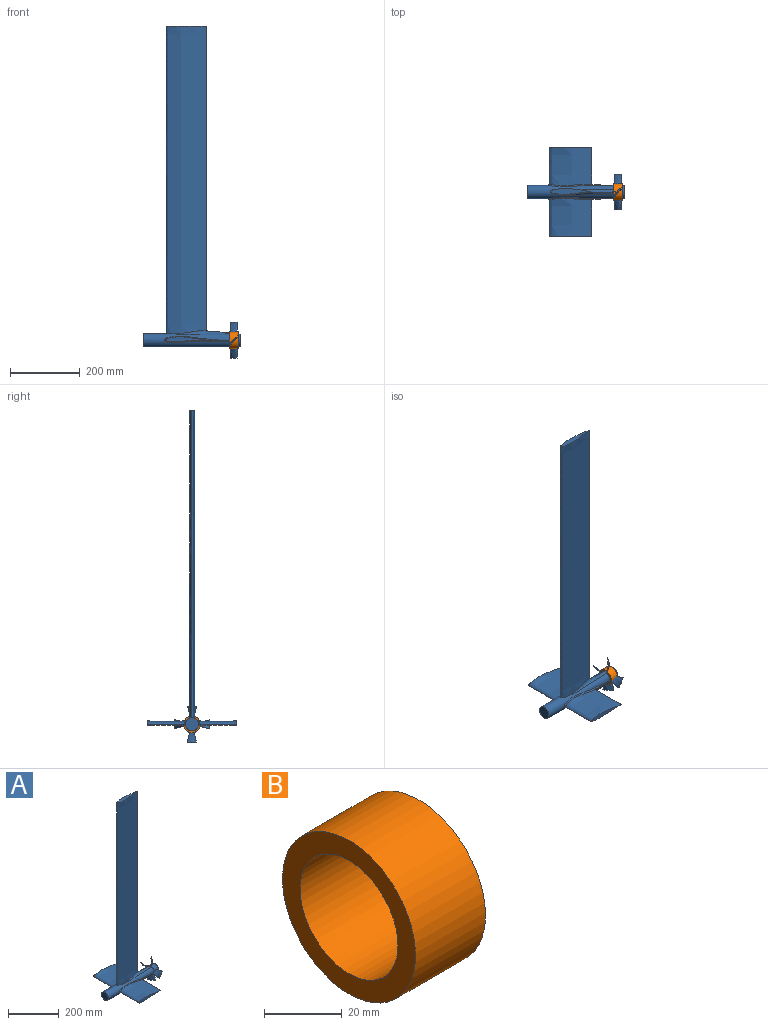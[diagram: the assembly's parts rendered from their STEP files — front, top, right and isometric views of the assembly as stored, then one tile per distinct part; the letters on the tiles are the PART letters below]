
ASSEMBLY  parts=2 mates=1
PART A: 35 faces, bbox 313.5x254.6x950.5 mm
  f0: plane 20.88x15.27mm, normal (1,0,0), area 34.3mm2, adj f6,f15,f21,f30,f32
  f1: plane 20.86x18.71mm, normal (1,0,0), area 44.7mm2, adj f6,f15,f20,f21,f27,f29
  f2: plane 20.54x15.24mm, normal (1,0,0), area 34.1mm2, adj f6,f21,f24,f26
  f3: extruded ~881.15x119.21mm, area 102994.5mm2, adj f4,f5,f15,f20
  f4: extruded ~880.11x115.56mm, area 103673mm2, adj f3,f5,f15
  f5: plane 115.59x15.95mm, normal (0,0,1), area 1218.9mm2, adj f3,f4
  f6: cylinder r=19.05mm len=254mm, axis (-1,0,0), area 23671.1mm2, adj f0,f1,f2,f7,f8,f15,f16,f17
  f7: plane 20.54x15.24mm, normal (1,0,0), area 34.1mm2, adj f6,f21,f23,f33
  f8: plane 38.1x38.1mm, normal (-1,0,0), area 1140.1mm2, adj f6
  f9: plane 120.65x12.89mm, normal (0,1,0), area 984.2mm2, adj f10,f11
  f10: extruded ~120.65x105.16mm, area 12739.2mm2, adj f9,f11,f16,f17
  f11: extruded ~120.65x104.46mm, area 12900mm2, adj f9,f10,f16
  f12: plane 120.67x12.89mm, normal (0,-1,0), area 984.2mm2, adj f13,f14
  f13: extruded ~120.65x105.16mm, area 12739.2mm2, adj f12,f14,f18,f19
  f14: extruded ~120.65x104.46mm, area 12900mm2, adj f12,f13,f19
  f15: bspline ~246.87x15.23mm, area 1459.2mm2, adj f0,f1,f3,f4,f6,f20,f29,f30
  f16: bspline ~202.66x19.82mm, area 667.5mm2, adj f6,f10,f11,f17
  f17: bspline ~228.56x6.02mm, area 809.6mm2, adj f6,f10,f16
  f18: bspline ~228.56x6.02mm, area 752.8mm2, adj f6,f13,f19,f32
  f19: bspline ~202.66x19.82mm, area 667.5mm2, adj f6,f13,f14,f18,f32
  f20: bspline ~193.83x13.44mm, area 947.7mm2, adj f1,f3,f6,f15
  f21: cylinder r=17.78mm len=35.56mm, axis (-1,0,0), area 2775.2mm2, adj f0,f1,f2,f7,f22,f23,f24,f26
  f22: plane 35.56x35.56mm, normal (1,0,0), area 993.1mm2, adj f21
  f23: bspline ~33.51x25.77mm, area 881.3mm2, adj f6,f7,f21,f24,f25
  f24: bspline ~50.8x25.79mm, area 873.7mm2, adj f2,f6,f21,f23,f25
  f25: plane 26.36x19.69mm, normal (0,0,-1), area 67.5mm2, adj f23,f24
  f26: bspline ~33.51x25.77mm, area 881.3mm2, adj f2,f6,f21,f27,f28
  f27: bspline ~50.8x25.79mm, area 873.7mm2, adj f1,f6,f21,f26,f28
  f28: plane 26.36x19.69mm, normal (0,1,0), area 67.5mm2, adj f26,f27
  f29: bspline ~33.51x25.77mm, area 878.8mm2, adj f1,f15,f21,f30,f31
  f30: bspline ~50.8x25.79mm, area 873mm2, adj f0,f15,f21,f29,f31
  f31: plane 26.01x19.34mm, normal (0,0,1), area 67.5mm2, adj f29,f30
  f32: bspline ~50.8x25.77mm, area 880.8mm2, adj f0,f6,f18,f19,f21,f33,f34
  f33: bspline ~50.8x25.79mm, area 873.7mm2, adj f6,f7,f21,f32,f34
  f34: plane 25.99x19.32mm, normal (0,-1,0), area 67.5mm2, adj f32,f33
PART B: 4 faces, bbox 25.4x48.3x48.3 mm
  f0: cylinder r=17.78mm len=35.56mm, axis (-1,0,0), area 2837.6mm2, adj f2,f3
  f1: cylinder r=24.13mm len=48.26mm, axis (-1,0,0), area 3851mm2, adj f2,f3
  f2: plane 48.26x48.26mm, normal (1,0,0), area 836.1mm2, adj f0,f1
  f3: plane 48.26x48.26mm, normal (-1,0,0), area 836.1mm2, adj f0,f1
PLACE A t=(-5.47,138.68,-69.43)mm
PLACE B t=(114.74,11.68,-69.43)mm
MATE cylindrical B.f0 <-> A.f21  axis (-1,0,0) through (127.44,11.68,-69.43)mm
